# Revit family: QF_ADVENTYS_ADV1527-C_V04_D2IC_6000
name_source: partatom
category: Attrezzature speciali
units: mm (PartAtom-declared; Revit-internal decimal feet)

## family parameters
Condiviso = No
Host = Superficie
Punto di calcolo locali = No
Quota connettore circolare = Usa diametro
Taglio con vuoti quando caricato = No
Tipo di parte = Normale

## types (1)
- ADV1527-C V04
    Controller_Height = 120 mm  [stored 0.393701 ft]
    Controller_Width = 394 mm
    Cycle = 50 Hz
    Depth = 580 mm  [stored 1.90289 ft]
    Depth Actual = 440 mm  [stored 1.44357 ft]
    Height = 162 mm  [stored 0.531496 ft]
    Height Actual = 162 mm  [stored 0.531496 ft]
    Item Number = ADV1527-C V04
    Length Actual = 580 mm  [stored 1.90289 ft]
    Modello = D2IC 6000
    Phase = 1
    Produttore = ADVENTYS
    Prospetto di default = 1219.2 mm  [stored 4 ft]
    URL = https://adventys.com
    Volts = 220 V
    Watts = 6000 W
    Weight = 13
    Width = 440 mm  [stored 1.44357 ft]

note: [stored X ft] marks values corroborated as IEEE doubles in the binary element streams (Revit-internal decimal feet)
